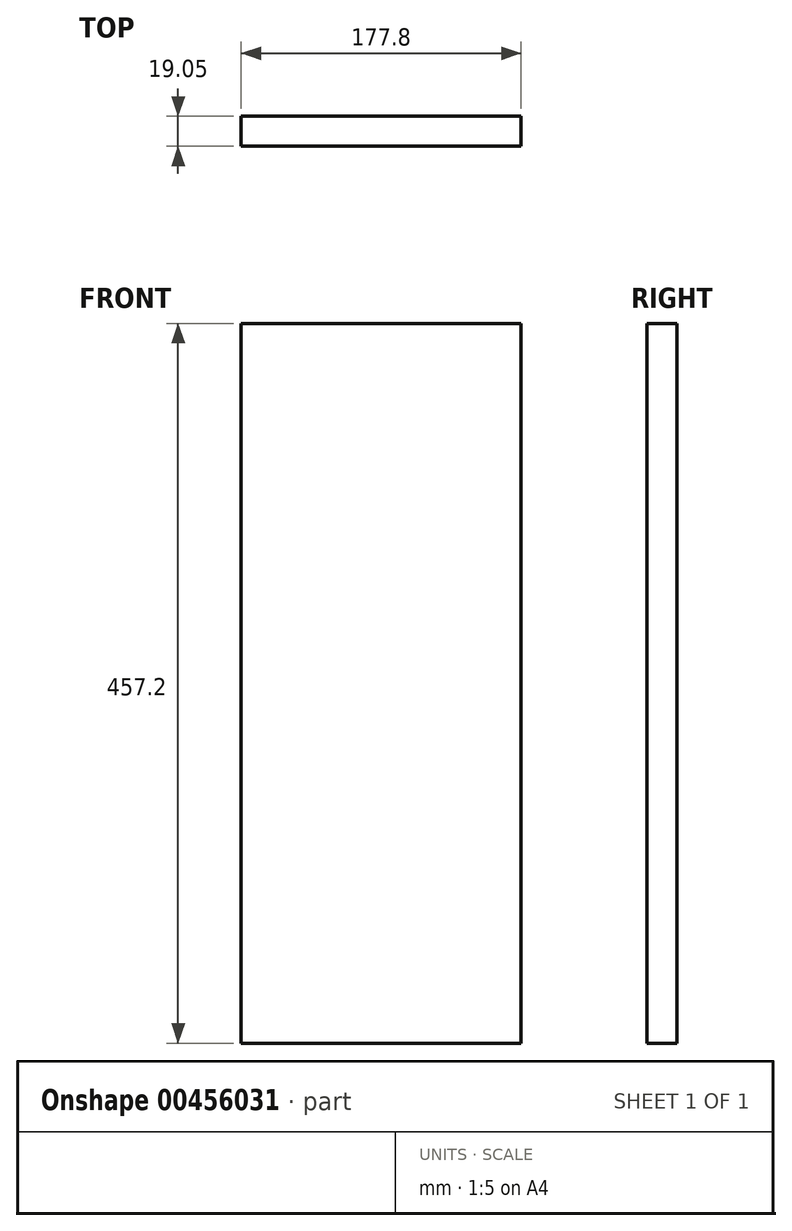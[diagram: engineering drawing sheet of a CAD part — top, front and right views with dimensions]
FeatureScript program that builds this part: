
annotation { "Feature Type Name" : "Feature", "Feature Type Description" : "" }
export const myFeature = defineFeature(function(context is Context, id is Id, definition is map)
    precondition{}
    {
        {
            var Q0;
            Q0=qCreatedBy(makeId("Top.planeOp"),FACE);
            var sketch = newSketch(context, id + "F0", { "sketchPlane" : qUnion([Q0])});
            skLineSegment(sketch, "E0.bottom", {"start": v(0, 0) * mm, "end": v(177.8, 0) * mm});
            skLineSegment(sketch, "E0.top", {"start": v(0, -19.05) * mm, "end": v(177.8, -19.05) * mm});
            skLineSegment(sketch, "E0.left", {"start": v(0, 0) * mm, "end": v(0, -19.05) * mm});
            skLineSegment(sketch, "E0.right", {"start": v(177.8, 0) * mm, "end": v(177.8, -19.05) * mm});
            skSolve(sketch);
        }
        {
            var Q0;
            Q0 = qSketchRegion(id + "F0", true);
            extrude(context, id + "F1", {"entities" : qUnion([Q0]), "depth" : 457.2 * mm});
        }
    });
